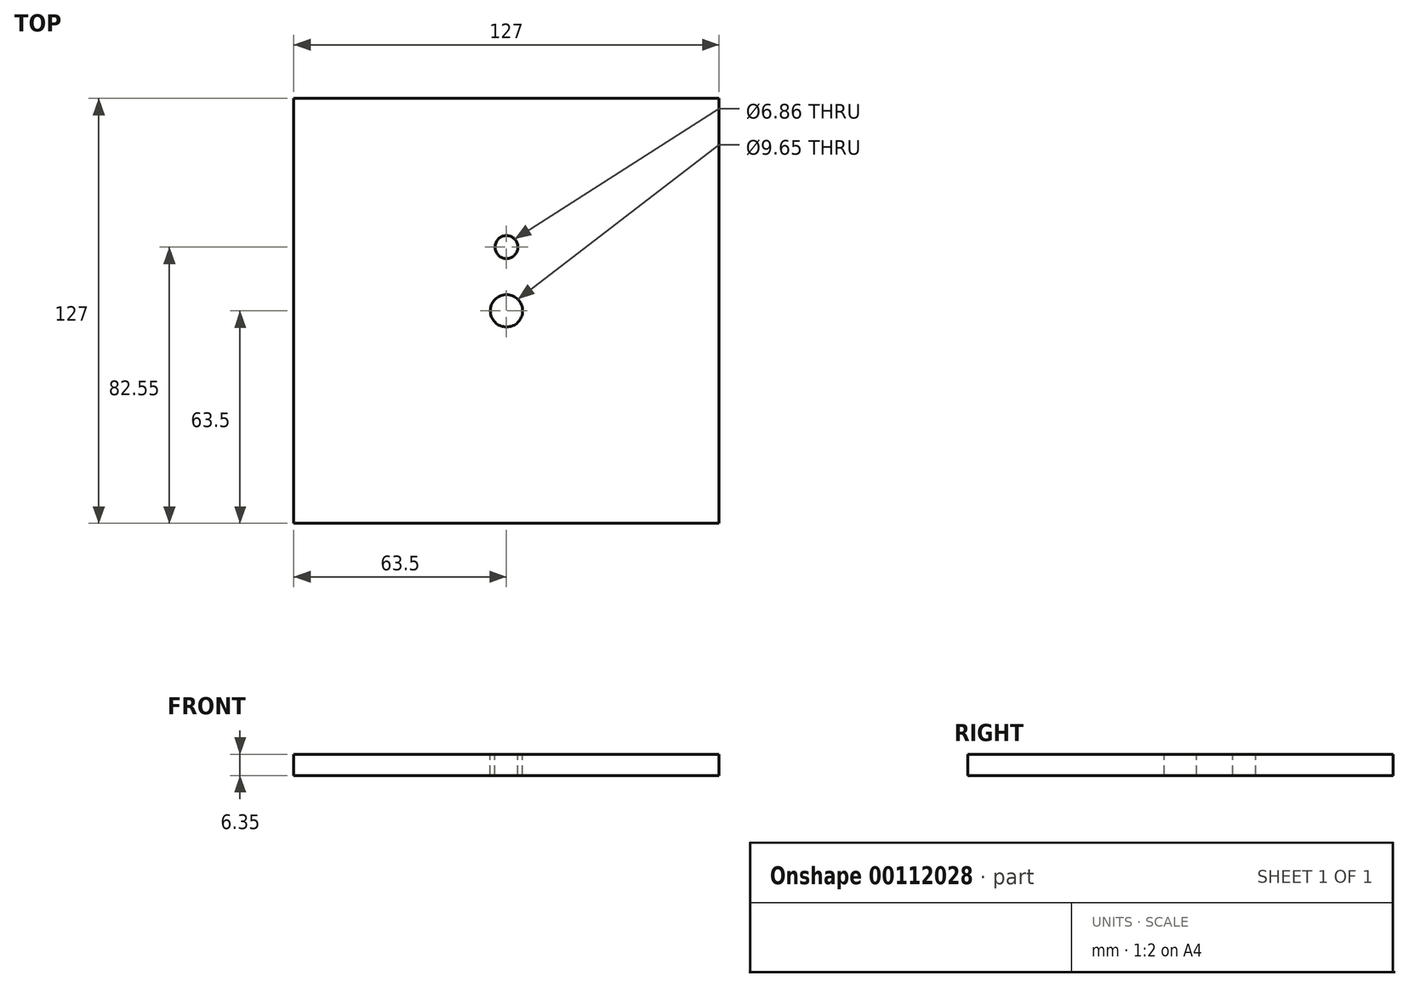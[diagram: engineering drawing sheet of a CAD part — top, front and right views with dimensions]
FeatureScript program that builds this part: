
annotation { "Feature Type Name" : "Feature", "Feature Type Description" : "" }
export const myFeature = defineFeature(function(context is Context, id is Id, definition is map)
    precondition{}
    {
        {
            var Q0;
            Q0=qCreatedBy(makeId("Top.planeOp"),FACE);
            var sketch = newSketch(context, id + "F0", { "sketchPlane" : qUnion([Q0])});
            skLineSegment(sketch, "E0", {"start": v(-63.5, 63.5) * mm, "end": v(-63.5, 0) * mm});
            skLineSegment(sketch, "E1", {"start": v(-63.5, 63.5) * mm, "end": v(0, 63.5) * mm});
            skLineSegment(sketch, "E2.MirrorCS", {"start": v(63.5, 63.5) * mm, "end": v(0, 63.5) * mm});
            skLineSegment(sketch, "E3.MirrorCS", {"start": v(63.5, 63.5) * mm, "end": v(63.5, 0) * mm});
            skLineSegment(sketch, "E4.MirrorCS", {"start": v(-63.5, -63.5) * mm, "end": v(-63.5, 0) * mm});
            skLineSegment(sketch, "E5.MirrorCS", {"start": v(-63.5, -63.5) * mm, "end": v(0, -63.5) * mm});
            skLineSegment(sketch, "E6.MirrorCS", {"start": v(63.5, -63.5) * mm, "end": v(0, -63.5) * mm});
            skLineSegment(sketch, "E7.MirrorCS", {"start": v(63.5, -63.5) * mm, "end": v(63.5, 0) * mm});
            skSolve(sketch);
        }
        {
            var Q0;
            Q0 = qSketchRegion(id + "F0", true);
            extrude(context, id + "F1", {"entities" : qUnion([Q0]), "depth" : 6.35 * mm});
        }
        {
            var Q0;
            Q0=makeQuery(id+"F1.opExtrude","CAP_FACE",FACE,{"disambiguationData":[OSD([sQuery(id+"F0.wireOp",EDGE,"E0"),sQuery(id+"F0.wireOp",EDGE,"E1"),sQuery(id+"F0.wireOp",EDGE,"E2.MirrorCS"),sQuery(id+"F0.wireOp",EDGE,"E3.MirrorCS"),sQuery(id+"F0.wireOp",EDGE,"E4.MirrorCS"),sQuery(id+"F0.wireOp",EDGE,"E5.MirrorCS"),sQuery(id+"F0.wireOp",EDGE,"E6.MirrorCS"),sQuery(id+"F0.wireOp",EDGE,"E7.MirrorCS")])],"isStart":false});
            var sketch = newSketch(context, id + "F2", { "sketchPlane" : qUnion([Q0])});
            skCircle(sketch, "E8", {"center": v(0, 0) * mm, "radius": 4.83 * mm});
            skCircle(sketch, "E9", {"center": v(0, 0) * mm, "radius": 19.05 * mm});
            skCircle(sketch, "E10", {"center": v(0, 19.05) * mm, "radius": 3.43 * mm});
            skSolve(sketch);
        }
        {
            var Q0;
            Q0=makeQuery(id+"F2.imprint","IMPRINT",FACE,{"disambiguationData":[TD([[makeQuery(id+"F2.imprint","IMPRINT",EDGE,{"derivedFrom":sQuery(id+"F2.wireOp",EDGE,"E8")}),1.0]])]});
            var Q1;
            {var subQ0=sQuery(id+"F2.wireOp",EDGE,"E10");var subQ1=sQuery(id+"F2.wireOp",EDGE,"E9");var subQ2=makeQuery(id+"F2.imprint","INTERSECT",VERTEX,{"disambiguationData":[OD(0.0)],"derivedFrom":[subQ1,subQ0]});Q1=makeQuery(id+"F2.imprint","IMPRINT",FACE,{"disambiguationData":[TD([[makeQuery(id+"F2.imprint","IMPRINT",EDGE,{"disambiguationData":[TD([[subQ2,1.0]])],"derivedFrom":subQ1}),1.0]])]});}
            var Q2;
            {var subQ0=sQuery(id+"F2.wireOp",EDGE,"E10");var subQ1=sQuery(id+"F2.wireOp",EDGE,"E9");var subQ2=makeQuery(id+"F2.imprint","INTERSECT",VERTEX,{"disambiguationData":[OD(0.0)],"derivedFrom":[subQ1,subQ0]});Q2=makeQuery(id+"F2.imprint","IMPRINT",FACE,{"disambiguationData":[TD([[makeQuery(id+"F2.imprint","IMPRINT",EDGE,{"disambiguationData":[TD([[subQ2,1.0]])],"derivedFrom":subQ1}),-1.0]])]});}
            extrude(context, id + "F3", {"entities" : qUnion([Q0, Q1, Q2]), "operationType" : NewBodyOperationType.REMOVE, "oppositeDirection" : true, "depth" : 25.4 * mm});
        }
    });
